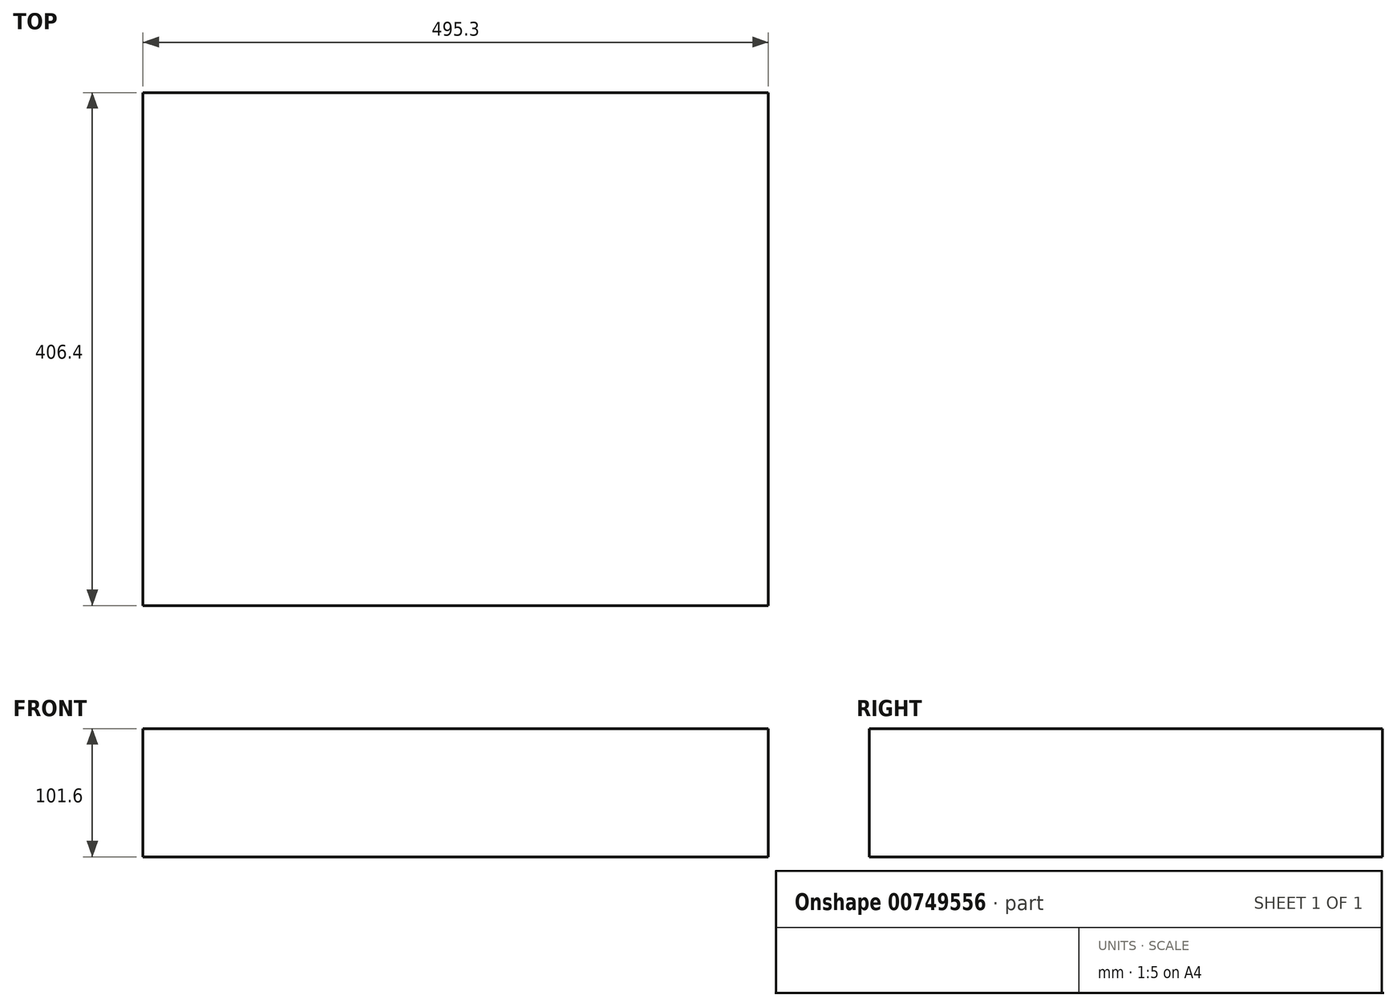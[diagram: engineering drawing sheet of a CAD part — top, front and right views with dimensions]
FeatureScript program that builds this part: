
annotation { "Feature Type Name" : "Feature", "Feature Type Description" : "" }
export const myFeature = defineFeature(function(context is Context, id is Id, definition is map)
    precondition{}
    {
        {
            var Q0;
            Q0=qCreatedBy(makeId("Top.planeOp"),FACE);
            var sketch = newSketch(context, id + "F0", { "sketchPlane" : qUnion([Q0])});
            skLineSegment(sketch, "E0.bottom", {"start": v(247.65, 203.2) * mm, "end": v(-247.65, 203.2) * mm});
            skLineSegment(sketch, "E0.top", {"start": v(247.65, -203.2) * mm, "end": v(-247.65, -203.2) * mm});
            skLineSegment(sketch, "E0.left", {"start": v(247.65, 203.2) * mm, "end": v(247.65, -203.2) * mm});
            skLineSegment(sketch, "E0.right", {"start": v(-247.65, 203.2) * mm, "end": v(-247.65, -203.2) * mm});
            skPoint(sketch, "E0.middle", {"position": v(0, 0) * mm});
            skSolve(sketch);
        }
        {
            var Q0;
            Q0=makeQuery(id+"F0.imprint","IMPRINT",FACE,{"disambiguationData":[TD([[makeQuery(id+"F0.imprint","IMPRINT",EDGE,{"derivedFrom":sQuery(id+"F0.wireOp",EDGE,"E0.bottom")}),1.0]])]});
            extrude(context, id + "F1", {"entities" : qUnion([Q0]), "depth" : 101.6 * mm, "offsetDistance" : 25.4 * mm});
        }
    });
